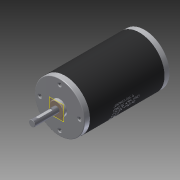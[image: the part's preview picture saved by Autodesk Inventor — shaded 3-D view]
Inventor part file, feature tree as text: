
AUTODESK INVENTOR PART (.ipt)
format: ipt  version: 2016 SP1 (Build 200210100, 210)  size: 7,276,544 bytes
history: native  units: mm (DEFAULTED — no unit token found)
features: sketch x10, extrude x7, chamfer x4, plane x3, hole x2, pattern_circular x2, fillet x2, emboss x1, split x1
ambient origin geometry x8: Origin, YZ Plane, XZ Plane, XY Plane, X Axis, Y Axis, Z Axis, Center Point
bodies: Solid1 (feature_tree), Solid2 (feature_tree), Solid3 (feature_tree)
feature tree (32):
  extrude  "Extrusion1"  Depth=7.0mm TaperAngle=0.0deg
  extrude  "Extrusion2"  Depth=3.9878mm TaperAngle=0.0deg
  chamfer  "Chamfer1"  Distance=1.0mm
  hole  "Hole2"  [1 undecoded]
  pattern_circular  "Circular Pattern2"  Count=4 Angle=90.0deg
  chamfer  "Chamfer3"  Distance=31.623mm
  extrude  "Extrusion3"  Depth=12.7mm
  fillet  "Fillet1"  Radius=64.4144mm
  extrude  "Extrusion5"  Depth=64.008mm
  extrude  "Extrusion6"  Depth=7.0mm
  extrude  "Extrusion7"  Depth=0.508mm
  hole  "Hole3"  [1 undecoded]
  chamfer  "Chamfer2"  Distance=20.0mm Angle=360.0deg
  pattern_circular  "Circular Pattern3"  [2 undecoded]
  fillet  "Fillet2"  [1 undecoded]
  chamfer  "Chamfer4"  Distance=1.99898mm
  plane  "Work Plane1"
  extrude  "Extrusion8"  Depth=1.99898mm
  plane  "Work Plane2"
  emboss  "Emboss1"
  plane  "Work Plane3"
  split  "Split1"
  sketch  "Sketch1"  dims[d0=64.008mm d1=7.0mm d2=0.0mm]
  sketch  "Sketch2"  dims[d3=19.05mm d4=3.9878mm d5=0.0mm d6=1.0mm d7=1.0mm]
  sketch  "Sketch4"  dims[d18=3.9624mm d19=9.525mm d20=6.35mm d21=60.0deg d22=19.05mm d23=20.594885mm d24=25.4mm d25=40.0mm d27=90.0deg]
  sketch  "Sketch5"  dims[d28=7.9502mm d29=31.623mm d30=0.0mm]
  sketch  "Sketch8"  dims[d31=0.79375mm d33=12.7mm d38=64.4144mm]
  sketch  "Sketch9"  dims[d39=95.6056mm d40=0.0mm d41=64.008mm]
  sketch  "Sketch10"  dims[d42=7.0mm d43=0.0mm d44=30.1498mm]
  sketch  "Sketch11"  dims[d45=4.1148mm d46=0.0mm]
  sketch  "Sketch12"  dims[d47=5.08mm d48=12.7mm d49=9.906mm d50=4.572mm d51=14.3117mm d52=7.62mm d53=20.594885mm d54=0.508mm d55=3.175mm]
  sketch  "Sketch13"  dims[d56=0.762mm d57=0.762mm d58=3.175mm d59=20.0mm d61=360.0deg d62=0.25mm d63=3.175mm d64=45.0deg d65=45.0deg d66=45.0deg d67=45.0deg d68=1.99898mm d70=20.09902mm d71=7.99338mm d72=1.15062mm d73=0.0mm d74=30.48mm d75=0.0254mm d76=0.0mm d77=0.0mm]
note: 5 required parameter values undecoded (feature->parameter linkage not recoverable at this tier; creation-order binding heuristic only, values carry confidence <= 0.55)
